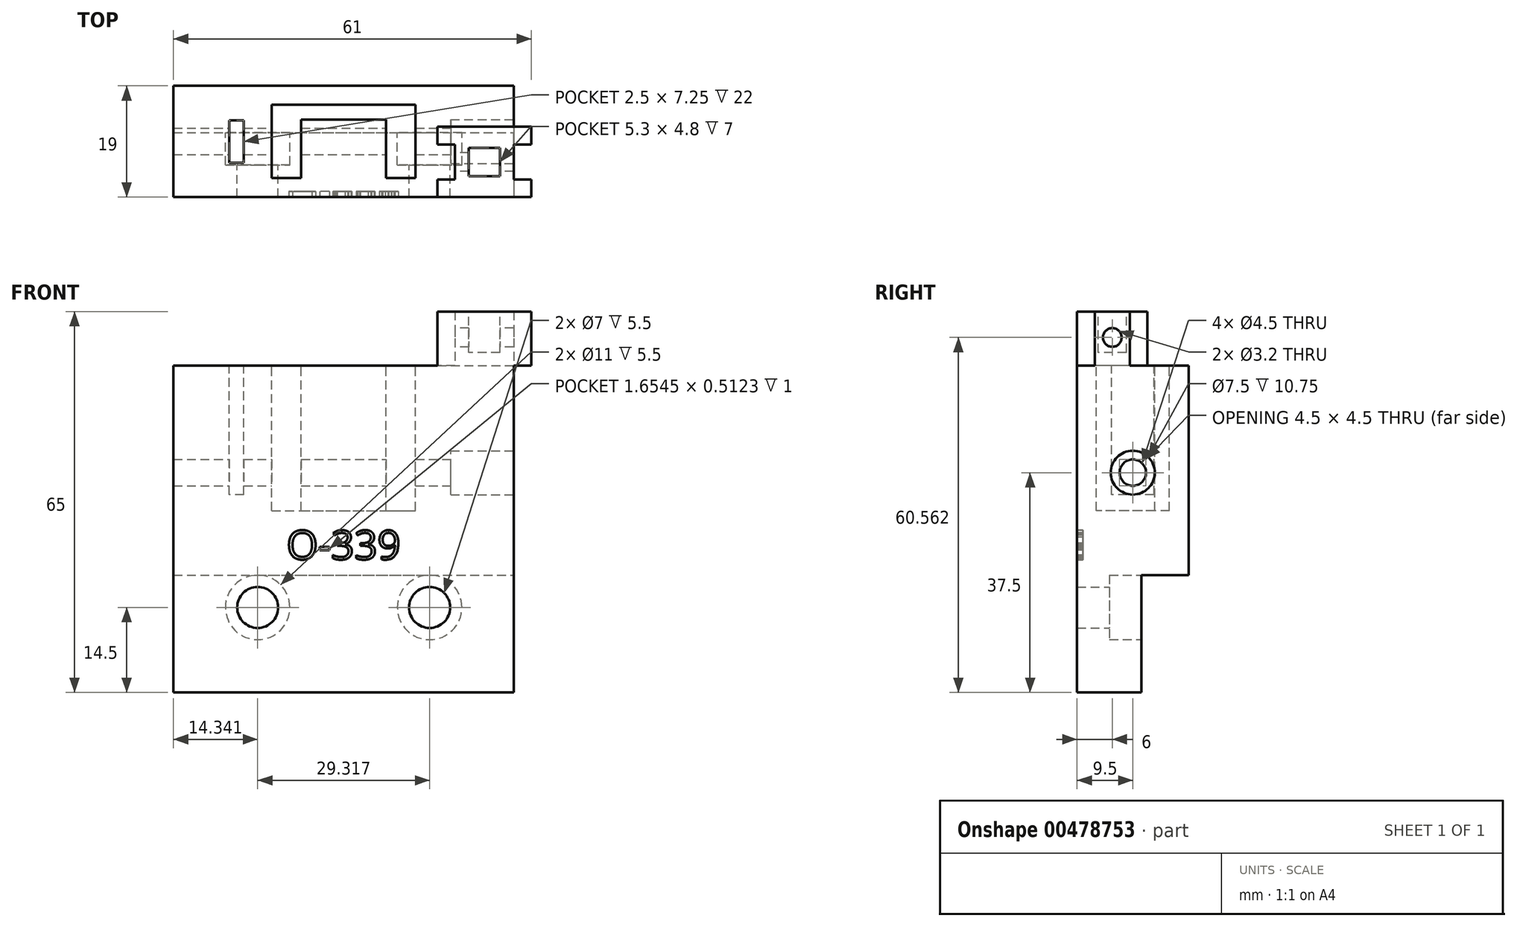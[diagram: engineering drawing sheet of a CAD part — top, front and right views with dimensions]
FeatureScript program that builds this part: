
annotation { "Feature Type Name" : "Feature", "Feature Type Description" : "" }
export const myFeature = defineFeature(function(context is Context, id is Id, definition is map)
    precondition{}
    {
        {
            var Q0;
            Q0=qCreatedBy(makeId("Top.planeOp"),FACE);
            var sketch = newSketch(context, id + "F0", { "sketchPlane" : qUnion([Q0])});
            skLineSegment(sketch, "E0.bottom", {"start": v(-29, 9.5) * mm, "end": v(29, 9.5) * mm});
            skLineSegment(sketch, "E0.top", {"start": v(-29, -9.5) * mm, "end": v(29, -9.5) * mm});
            skLineSegment(sketch, "E0.left", {"start": v(-29, 9.5) * mm, "end": v(-29, -9.5) * mm});
            skLineSegment(sketch, "E0.right", {"start": v(29, 9.5) * mm, "end": v(29, -9.5) * mm});
            skSolve(sketch);
        }
        {
            var Q0;
            Q0=qSketchRegion(id+"F0",true);
            extrude(context, id + "F1", {"entities" : qUnion([Q0]), "depth" : 11 * mm});
        }
        {
            var Q0;
            Q0=makeQuery(id+"F1.opExtrude","CAP_FACE",FACE,{"disambiguationData":[OSD([sQuery(id+"F0.wireOp",EDGE,"E0.bottom"),sQuery(id+"F0.wireOp",EDGE,"E0.top"),sQuery(id+"F0.wireOp",EDGE,"E0.left"),sQuery(id+"F0.wireOp",EDGE,"E0.right"),sQuery(id+"F0.wireOp",EDGE,"AuSHMrTt-jpj0-5Ru2-xaIe-a4Oixfi13iDE"),sQuery(id+"F0.wireOp",EDGE,"9J5HWsQ0-lQpk-E1t6-wWkI-SOKKZm0BYfsw"),sQuery(id+"F0.wireOp",EDGE,"2GzKSPJo-uI2N-Esed-kJXd-WJqO7sIm6bVz"),sQuery(id+"F0.wireOp",EDGE,"DJKESrdY-mQTo-sUHj-6MfV-pHmhVGQO2tIG")])],"isStart":false});
            var sketch = newSketch(context, id + "F2", { "sketchPlane" : qUnion([Q0])});
            skLineSegment(sketch, "E1.bottom", {"start": v(-29, 9.5) * mm, "end": v(29, 9.5) * mm});
            skLineSegment(sketch, "E1.top", {"start": v(-29, -9.5) * mm, "end": v(29, -9.5) * mm});
            skLineSegment(sketch, "E1.left", {"start": v(-29, 9.5) * mm, "end": v(-29, -9.5) * mm});
            skLineSegment(sketch, "E1.right", {"start": v(29, 9.5) * mm, "end": v(29, -9.5) * mm});
            skPoint(sketch, "E1.middle", {"position": v(0, 0) * mm});
            skSolve(sketch);
        }
        {
            var Q0;
            Q0=qSketchRegion(id+"F2",true);
            extrude(context, id + "F3", {"entities" : qUnion([Q0]), "operationType" : NewBodyOperationType.ADD, "depth" : 24.75 * mm});
        }
        {
            var Q0;
            Q0=makeQuery(id+"F3.opExtrude","CAP_FACE",FACE,{"disambiguationData":[OSD([sQuery(id+"F2.wireOp",EDGE,"E1.bottom"),sQuery(id+"F2.wireOp",EDGE,"E1.top"),sQuery(id+"F2.wireOp",EDGE,"E1.left"),sQuery(id+"F2.wireOp",EDGE,"E1.right")])],"isStart":false});
            var sketch = newSketch(context, id + "F4", { "sketchPlane" : qUnion([Q0])});
            skLineSegment(sketch, "E2.bottom", {"start": v(-12.25, 6.25) * mm, "end": v(-7.25, 6.25) * mm});
            skLineSegment(sketch, "E2.top", {"start": v(-12.25, -6.25) * mm, "end": v(-7.25, -6.25) * mm});
            skLineSegment(sketch, "E2.left", {"start": v(-12.25, 6.25) * mm, "end": v(-12.25, -6.25) * mm});
            skLineSegment(sketch, "E2.right", {"start": v(-7.25, 6.25) * mm, "end": v(-7.25, -6.25) * mm});
            skPoint(sketch, "E2.middle", {"position": v(-9.75, 0) * mm});
            skLineSegment(sketch, "E3.bottom", {"start": v(7.25, 6.25) * mm, "end": v(12.25, 6.25) * mm});
            skLineSegment(sketch, "E3.top", {"start": v(7.25, -6.25) * mm, "end": v(12.25, -6.25) * mm});
            skLineSegment(sketch, "E3.left", {"start": v(7.25, 6.25) * mm, "end": v(7.25, -6.25) * mm});
            skLineSegment(sketch, "E3.right", {"start": v(12.25, 6.25) * mm, "end": v(12.25, -6.25) * mm});
            skPoint(sketch, "E3.middle", {"position": v(9.75, 0) * mm});
            skSolve(sketch);
        }
        {
            var Q0;
            Q0=qSketchRegion(id+"F4",true);
            extrude(context, id + "F5", {"entities" : qUnion([Q0]), "operationType" : NewBodyOperationType.REMOVE, "oppositeDirection" : true, "depth" : 24.75 * mm});
        }
        {
            var Q0;
            Q0=makeQuery(id+"F3.boolean.opBoolean","MERGE",FACE,{"derivedFrom":[makeQuery(id+"F1.opExtrude","SWEPT_FACE",FACE,{"disambiguationData":[OSD([sQuery(id+"F0.wireOp",EDGE,"E0.right")])]}),makeQuery(id+"F3.opExtrude","SWEPT_FACE",FACE,{"disambiguationData":[OSD([sQuery(id+"F2.wireOp",EDGE,"E1.right")])]})]});
            var sketch = newSketch(context, id + "F6", { "sketchPlane" : qUnion([Q0])});
            skCircle(sketch, "E4", {"center": v(0, 17.5) * mm, "radius": 2.25 * mm});
            skSolve(sketch);
        }
        {
            var Q0;
            Q0=qSketchRegion(id+"F6",true);
            extrude(context, id + "F7", {"entities" : qUnion([Q0]), "operationType" : NewBodyOperationType.REMOVE, "endBound" : BoundingType.THROUGH_ALL, "oppositeDirection" : true, "depth" : 53 * mm});
        }
        {
            var Q0;
            Q0=makeQuery(id+"F3.opExtrude","CAP_FACE",FACE,{"disambiguationData":[OSD([sQuery(id+"F2.wireOp",EDGE,"E1.bottom"),sQuery(id+"F2.wireOp",EDGE,"E1.top"),sQuery(id+"F2.wireOp",EDGE,"E1.left"),sQuery(id+"F2.wireOp",EDGE,"E1.right")])],"isStart":false});
            var sketch = newSketch(context, id + "F8", { "sketchPlane" : qUnion([Q0])});
            skLineSegment(sketch, "E5.bottom", {"start": v(-7.25, 6.25) * mm, "end": v(7.25, 6.25) * mm});
            skLineSegment(sketch, "E5.top", {"start": v(-7.25, 3.75) * mm, "end": v(7.25, 3.75) * mm});
            skLineSegment(sketch, "E5.left", {"start": v(-7.25, 6.25) * mm, "end": v(-7.25, 3.75) * mm});
            skLineSegment(sketch, "E5.right", {"start": v(7.25, 6.25) * mm, "end": v(7.25, 3.75) * mm});
            skSolve(sketch);
        }
        {
            var Q0;
            Q0=qSketchRegion(id+"F8",true);
            extrude(context, id + "F9", {"entities" : qUnion([Q0]), "operationType" : NewBodyOperationType.REMOVE, "oppositeDirection" : true, "depth" : 24.75 * mm});
        }
        {
            var Q0;
            Q0=makeQuery(id+"F3.boolean.opBoolean","MERGE",FACE,{"derivedFrom":[makeQuery(id+"F1.opExtrude","SWEPT_FACE",FACE,{"disambiguationData":[OSD([sQuery(id+"F0.wireOp",EDGE,"E0.right")])]}),makeQuery(id+"F3.opExtrude","SWEPT_FACE",FACE,{"disambiguationData":[OSD([sQuery(id+"F2.wireOp",EDGE,"E1.right")])]})]});
            var sketch = newSketch(context, id + "F10", { "sketchPlane" : qUnion([Q0])});
            skCircle(sketch, "E6", {"center": v(0, 17.5) * mm, "radius": 3.75 * mm});
            skSolve(sketch);
        }
        {
            var Q0;
            Q0=qSketchRegion(id+"F10",true);
            extrude(context, id + "F11", {"entities" : qUnion([Q0]), "operationType" : NewBodyOperationType.REMOVE, "oppositeDirection" : true, "depth" : 10.75 * mm});
        }
        {
            var Q0;
            Q0=makeQuery(id+"F3.opExtrude","CAP_FACE",FACE,{"disambiguationData":[OSD([sQuery(id+"F2.wireOp",EDGE,"E1.bottom"),sQuery(id+"F2.wireOp",EDGE,"E1.top"),sQuery(id+"F2.wireOp",EDGE,"E1.left"),sQuery(id+"F2.wireOp",EDGE,"E1.right")])],"isStart":false});
            var sketch = newSketch(context, id + "F12", { "sketchPlane" : qUnion([Q0])});
            skLineSegment(sketch, "E7.bottom", {"start": v(-17, 3.63) * mm, "end": v(-19.5, 3.63) * mm});
            skLineSegment(sketch, "E7.top", {"start": v(-17, -3.62) * mm, "end": v(-19.5, -3.62) * mm});
            skLineSegment(sketch, "E7.left", {"start": v(-17, 3.63) * mm, "end": v(-17, -3.62) * mm});
            skLineSegment(sketch, "E7.right", {"start": v(-19.5, 3.63) * mm, "end": v(-19.5, -3.62) * mm});
            skPoint(sketch, "E7.middle", {"position": v(-18.25, 0) * mm});
            skSolve(sketch);
        }
        {
            var Q0;
            Q0 = qSketchRegion(id + "F12", true);
            extrude(context, id + "F13", {"entities" : qUnion([Q0]), "operationType" : NewBodyOperationType.REMOVE, "oppositeDirection" : true, "depth" : 22 * mm});
        }
        {
            var Q0;
            Q0=makeQuery(id+"F1.opExtrude","SWEPT_FACE",FACE,{"disambiguationData":[OSD([sQuery(id+"F0.wireOp",EDGE,"E0.top")])]});
            var sketch = newSketch(context, id + "F14", { "sketchPlane" : qUnion([Q0])});
            skText(sketch, "E8", { "text": "O-339", "fontName": "OpenSans-Regular.ttf"});
            const initialGuessF14  = {"E8": [-0.00974, 0.0027, 1, 0, 0.00497]};
            skSetInitialGuess(sketch, initialGuessF14);
            skSolve(sketch);
        }
        {
            var Q0;
            Q0 = qSketchRegion(id + "F14", true);
            extrude(context, id + "F15", {"entities" : qUnion([Q0]), "operationType" : NewBodyOperationType.REMOVE, "oppositeDirection" : true, "depth" : 1 * mm});
        }
        {
            var Q0;
            Q0=makeQuery(id+"F3.opExtrude","CAP_FACE",FACE,{"disambiguationData":[OSD([sQuery(id+"F2.wireOp",EDGE,"E1.bottom"),sQuery(id+"F2.wireOp",EDGE,"E1.top"),sQuery(id+"F2.wireOp",EDGE,"E1.left"),sQuery(id+"F2.wireOp",EDGE,"E1.right")])],"isStart":false});
            var sketch = newSketch(context, id + "F16", { "sketchPlane" : qUnion([Q0])});
            skLineSegment(sketch, "E9.right", {"start": v(29, -0.5) * mm, "end": v(29, -6.5) * mm});
            skPoint(sketch, "E9.middle", {"position": v(24, -3.5) * mm});
            skLineSegment(sketch, "E10", {"start": v(19, -0.5) * mm, "end": v(19, -6.5) * mm});
            skLineSegment(sketch, "E11", {"start": v(19, -0.5) * mm, "end": v(16, -0.5) * mm});
            skLineSegment(sketch, "E12", {"start": v(16, -0.5) * mm, "end": v(16, 2.5) * mm});
            skLineSegment(sketch, "E13", {"start": v(16, 2.5) * mm, "end": v(32, 2.5) * mm});
            skLineSegment(sketch, "E14", {"start": v(32, 2.5) * mm, "end": v(32, -0.5) * mm});
            skLineSegment(sketch, "E15", {"start": v(32, -0.5) * mm, "end": v(29, -0.5) * mm});
            skLineSegment(sketch, "E16", {"start": v(19, -6.5) * mm, "end": v(16, -6.5) * mm});
            skLineSegment(sketch, "E17", {"start": v(16, -6.5) * mm, "end": v(16, -9.5) * mm});
            skLineSegment(sketch, "E18", {"start": v(16, -9.5) * mm, "end": v(32, -9.5) * mm});
            skLineSegment(sketch, "E19", {"start": v(32, -9.5) * mm, "end": v(32, -6.5) * mm});
            skLineSegment(sketch, "E20", {"start": v(32, -6.5) * mm, "end": v(29, -6.5) * mm});
            skSolve(sketch);
        }
        {
            var Q0;
            Q0 = qSketchRegion(id + "F16", true);
            extrude(context, id + "F17", {"entities" : qUnion([Q0]), "operationType" : NewBodyOperationType.ADD, "depth" : 9.25 * mm});
        }
        {
            var Q0;
            Q0=makeQuery(id+"F17.opExtrude","SWEPT_FACE",FACE,{"disambiguationData":[OSD([sQuery(id+"F16.wireOp",EDGE,"E10")])]});
            var sketch = newSketch(context, id + "F18", { "sketchPlane" : qUnion([Q0])});
            skCircle(sketch, "E21", {"center": v(3.5, 40.56) * mm, "radius": 1.6 * mm});
            skPoint(sketch, "E21.centerSnap0", {"position": v(3.5, 45) * mm});
            skSolve(sketch);
        }
        {
            var Q0;
            Q0=makeQuery(id+"F18.imprint","IMPRINT",FACE,{"disambiguationData":[TD([[makeQuery(id+"F18.imprint","IMPRINT",EDGE,{"derivedFrom":sQuery(id+"F18.wireOp",EDGE,"E21")}),1.0]])]});
            extrude(context, id + "F19", {"entities" : qUnion([Q0]), "operationType" : NewBodyOperationType.REMOVE, "endBound" : BoundingType.THROUGH_ALL, "oppositeDirection" : true, "depth" : 25 * mm});
        }
        {
            var Q0;
            Q0=makeQuery(id+"F17.opExtrude","CAP_FACE",FACE,{"disambiguationData":[OSD([sQuery(id+"F16.wireOp",EDGE,"E9.right"),sQuery(id+"F16.wireOp",EDGE,"E10"),sQuery(id+"F16.wireOp",EDGE,"E11"),sQuery(id+"F16.wireOp",EDGE,"E12"),sQuery(id+"F16.wireOp",EDGE,"E13"),sQuery(id+"F16.wireOp",EDGE,"E14"),sQuery(id+"F16.wireOp",EDGE,"E15"),sQuery(id+"F16.wireOp",EDGE,"E16"),sQuery(id+"F16.wireOp",EDGE,"E17"),sQuery(id+"F16.wireOp",EDGE,"E18"),sQuery(id+"F16.wireOp",EDGE,"E19"),sQuery(id+"F16.wireOp",EDGE,"E20")])],"isStart":false});
            var sketch = newSketch(context, id + "F20", { "sketchPlane" : qUnion([Q0])});
            skLineSegment(sketch, "E22.bottom", {"start": v(26.65, -1.1) * mm, "end": v(21.35, -1.1) * mm});
            skLineSegment(sketch, "E22.top", {"start": v(26.65, -5.9) * mm, "end": v(21.35, -5.9) * mm});
            skLineSegment(sketch, "E22.left", {"start": v(26.65, -1.1) * mm, "end": v(26.65, -5.9) * mm});
            skLineSegment(sketch, "E22.right", {"start": v(21.35, -1.1) * mm, "end": v(21.35, -5.9) * mm});
            skPoint(sketch, "E22.middle", {"position": v(24, -3.5) * mm});
            skPoint(sketch, "E22.middle.positionSnap0", {"position": v(29, -3.5) * mm});
            skPoint(sketch, "E22.middle.positionSnap1", {"position": v(24, -9.5) * mm});
            skPoint(sketch, "E22.centerSnap0", {"position": v(29, -3.5) * mm});
            skPoint(sketch, "E22.centerSnap1", {"position": v(24, -9.5) * mm});
            skSolve(sketch);
        }
        {
            var Q0;
            Q0 = qSketchRegion(id + "F20", true);
            extrude(context, id + "F21", {"entities" : qUnion([Q0]), "operationType" : NewBodyOperationType.REMOVE, "oppositeDirection" : true, "depth" : 7 * mm});
        }
        {
            var Q0;
            {var subQ1=sQuery(id+"F0.wireOp",EDGE,"E0.left");var subQ2=sQuery(id+"F0.wireOp",EDGE,"E0.top");var subQ5=sQuery(id+"F2.wireOp",EDGE,"E1.top");Q0=makeQuery(id+"F17.boolean.opBoolean","MERGE",FACE,{"derivedFrom":[makeQuery(id+"F15.boolean.opBoolean","SPLIT",FACE,{"disambiguationData":[TD([makeQuery(id+"F1.opExtrude","SWEPT_FACE",FACE,{"disambiguationData":[OSD([subQ1])]})])],"derivedFrom":makeQuery(id+"F3.boolean.opBoolean","MERGE",FACE,{"derivedFrom":[makeQuery(id+"F1.opExtrude","SWEPT_FACE",FACE,{"disambiguationData":[OSD([subQ2])]}),makeQuery(id+"F3.opExtrude","SWEPT_FACE",FACE,{"disambiguationData":[OSD([subQ5])]})]})}),makeQuery(id+"F17.opExtrude","SWEPT_FACE",FACE,{"disambiguationData":[OSD([sQuery(id+"F16.wireOp",EDGE,"E18")])]})]});}
            var sketch = newSketch(context, id + "F22", { "sketchPlane" : qUnion([Q0])});
            skLineSegment(sketch, "E23.bottom", {"start": v(-29, 0) * mm, "end": v(29, 0) * mm});
            skLineSegment(sketch, "E23.top", {"start": v(-29, -20) * mm, "end": v(29, -20) * mm});
            skLineSegment(sketch, "E23.left", {"start": v(-29, 0) * mm, "end": v(-29, -20) * mm});
            skLineSegment(sketch, "E23.right", {"start": v(29, 0) * mm, "end": v(29, -20) * mm});
            skSolve(sketch);
        }
        {
            var Q0;
            Q0 = qSketchRegion(id + "F22", true);
            extrude(context, id + "F23", {"entities" : qUnion([Q0]), "operationType" : NewBodyOperationType.ADD, "oppositeDirection" : true, "depth" : 11 * mm});
        }
        {
            var Q0;
            Q0=makeQuery(id+"F23.opExtrude","CAP_FACE",FACE,{"disambiguationData":[OSD([sQuery(id+"F22.wireOp",EDGE,"E23.bottom"),sQuery(id+"F22.wireOp",EDGE,"E23.top"),sQuery(id+"F22.wireOp",EDGE,"E23.left"),sQuery(id+"F22.wireOp",EDGE,"E23.right")])],"isStart":false});
            var sketch = newSketch(context, id + "F24", { "sketchPlane" : qUnion([Q0])});
            skCircle(sketch, "E24", {"center": v(-14.66, -5.5) * mm, "radius": 3.5 * mm});
            skCircle(sketch, "E25", {"center": v(14.66, -5.5) * mm, "radius": 3.5 * mm});
            skSolve(sketch);
        }
        {
            var Q0;
            Q0 = qSketchRegion(id + "F24", true);
            extrude(context, id + "F25", {"entities" : qUnion([Q0]), "operationType" : NewBodyOperationType.REMOVE, "endBound" : BoundingType.THROUGH_ALL, "oppositeDirection" : true, "depth" : 25 * mm});
        }
        {
            var Q0;
            Q0=makeQuery(id+"F23.opExtrude","CAP_FACE",FACE,{"disambiguationData":[OSD([sQuery(id+"F22.wireOp",EDGE,"E23.bottom"),sQuery(id+"F22.wireOp",EDGE,"E23.top"),sQuery(id+"F22.wireOp",EDGE,"E23.left"),sQuery(id+"F22.wireOp",EDGE,"E23.right")])],"isStart":false});
            var sketch = newSketch(context, id + "F26", { "sketchPlane" : qUnion([Q0])});
            skCircle(sketch, "E26", {"center": v(-14.66, -5.5) * mm, "radius": 5.5 * mm});
            skCircle(sketch, "E27", {"center": v(14.66, -5.5) * mm, "radius": 5.5 * mm});
            skSolve(sketch);
        }
        {
            var Q0;
            Q0 = qSketchRegion(id + "F26", true);
            extrude(context, id + "F27", {"entities" : qUnion([Q0]), "operationType" : NewBodyOperationType.REMOVE, "oppositeDirection" : true, "depth" : 5.5 * mm});
        }
    });
